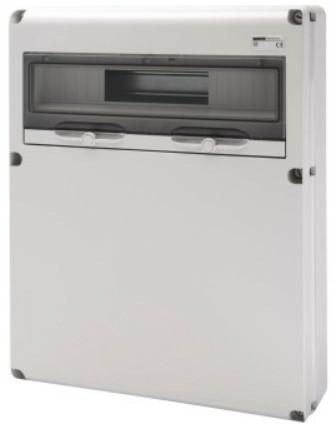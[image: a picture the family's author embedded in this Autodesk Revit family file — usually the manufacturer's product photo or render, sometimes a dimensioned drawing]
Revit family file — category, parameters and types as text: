
# Revit family: Building-IEC309Boards-GEWISS-68QDIN-DISTRIBUTION-BOARD-20MOD_BLANK
name_source: partatom
category: Apparecchi elettrici
units: mm (PartAtom-declared; Revit-internal decimal feet)

## family parameters
Condiviso = No
Host = Superficie
Mantenere orientamento annotazione = Sì
Punto di calcolo locali = Sì
Quota connettore circolare = Usa diametro
Taglio con vuoti quando caricato = No
Tipo di parte = Normale

## types (1)
- GW68012N - Q-DIN 20M BLIND COV. 560x450x135 IP65
    Accordance with Standards = EN 60208 - EN 60670-1 - IEC 60670-24
    Catalogue = BUILDING
    Catalogue Range = 68 QDIN
    Colour = Grey RAL 7035
    Descrizione = Q-DIN 20M BLIND COV. 560x450x135 IP65
    Dispersible power A (W) = 30
    Dispersible power B (W) = 92
    EAN code = 8011564744820
    Electrocod = 2242
    Glow Wire Test = 650°C
    Houseable socket = Blank lid
    IDF = 2b8a1711-d5c4-4269-b05b-5eb5a256160b
    IDT = 91d94f96-0e3b-43d6-a2ed-d5af9a5ddb7e
    IP degree = IP65
    Immagine tipo = GW68012N.jpg
    Installation type = Surface-mounting
    Insulation class = II
    L_Moduli = 380 mm  [stored 1.24672 ft]
    Modello = GW68012N
    N_Moduli = 20 mm  [stored 0.0656168 ft]
    No. of modules EN 50022 = 20
    No. of provided blank lids = -
    Operating temperature: = -25 +40 °C
    POMELLO = bianco
    PRESA = rosso
    Produttore = GEWISS S.p.A.
    Prospetto di default = 1219 mm
    SEO = Board
    STRUTTURA = RAL - 7035
    STRUTTURA ALTA = Poche
    Shock resistance = IK09
    Spostamento_S = 1000 mm  [stored 3.28084 ft]
    Technical sheet = https://www.gewiss.com
    Thermo-pressure with ball = 70
    URL = https://www.gewiss.com
    VETRO = Vetro
    Version file RFA = 21.5
    Version type = Empty

note: source unit labels omitted for Thermo-pressure with ball — the stored unit's dimension contradicts the parameter name (converter mislabeling)

note: [stored X ft] marks values corroborated as IEEE doubles in the binary element streams (Revit-internal decimal feet)

## geometry (parser evidence)
native form markers: Sweep x4
no freeform markers — native parametric forms only
